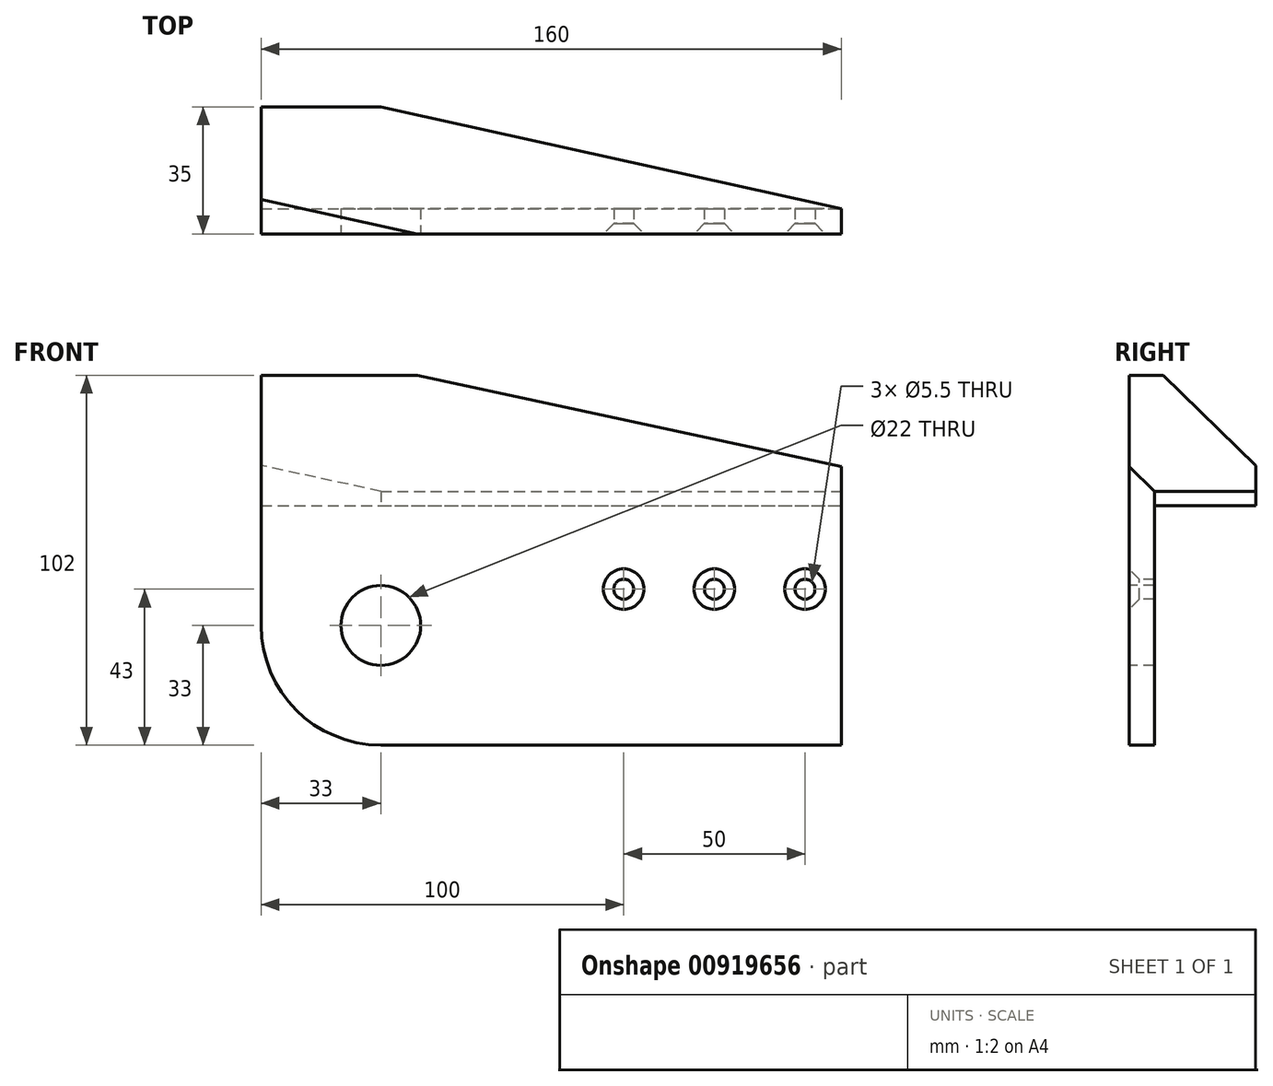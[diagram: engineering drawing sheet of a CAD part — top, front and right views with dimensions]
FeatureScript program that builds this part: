
annotation { "Feature Type Name" : "Feature", "Feature Type Description" : "" }
export const myFeature = defineFeature(function(context is Context, id is Id, definition is map)
    precondition{}
    {
        {
            var Q0;
            Q0=qCreatedBy(makeId("Front.planeOp"),FACE);
            var sketch = newSketch(context, id + "F0", { "sketchPlane" : qUnion([Q0])});
            skCircle(sketch, "E0", {"center": v(0, 0) * mm, "radius": 11 * mm});
            skLineSegment(sketch, "E1", {"start": v(127, -33) * mm, "end": v(0, -33) * mm});
            skLineSegment(sketch, "E2.right", {"start": v(127, 33) * mm, "end": v(127, -33) * mm});
            skLineSegment(sketch, "E3", {"start": v(67, 10) * mm, "end": v(117, 10) * mm, "construction": true});
            skPoint(sketch, "E4", {"position": v(92, 10) * mm});
            skCircle(sketch, "E5", {"center": v(67, 10) * mm, "radius": 2.5 * mm});
            skCircle(sketch, "E6", {"center": v(92, 10) * mm, "radius": 2.5 * mm});
            skCircle(sketch, "E7", {"center": v(117, 10) * mm, "radius": 2.5 * mm});
            skLineSegment(sketch, "E8", {"start": v(-33, 0) * mm, "end": v(-33, 33) * mm});
            skArc(sketch, "E9", {"start": v(0, -33) * mm, "mid": v(-23.33, -23.33) * mm, "end": v(-33, 0) * mm});
            skLineSegment(sketch, "E10", {"start": v(-33, 33) * mm, "end": v(127, 33) * mm});
            skCircle(sketch, "E11", {"center": v(0, 0) * mm, "radius": 33 * mm, "construction": true});
            skSolve(sketch);
        }
        {
            var Q0;
            Q0=makeQuery(id+"F0.imprint","IMPRINT",FACE,{"disambiguationData":[TD([[makeQuery(id+"F0.imprint","IMPRINT",EDGE,{"derivedFrom":sQuery(id+"F0.wireOp",EDGE,"E0")}),-1.0]])]});
            extrude(context, id + "F1", {"entities" : qUnion([Q0]), "oppositeDirection" : true, "depth" : 7 * mm, "offsetDistance" : 25 * mm});
        }
        {
            var Q0;
            Q0=sQuery(id+"F0.wireOp",VERTEX,"E3.end");
            var Q1;
            Q1=sQuery(id+"F0.wireOp",VERTEX,"E4");
            var Q2;
            Q2=sQuery(id+"F0.wireOp",VERTEX,"E3.start");
            var Q3;
            Q3=makeQuery(id+"F1.opExtrude","SWEPT_BODY",BODY,{"disambiguationData":[OSD([sQuery(id+"F0.wireOp",EDGE,"E0"),sQuery(id+"F0.wireOp",EDGE,"NhK39m2a-VStp-sb5Q-2b8d-sSrkkGbPDMdk.bottom"),sQuery(id+"F0.wireOp",EDGE,"Ms3glqPk-d3eh-z7h0-pjau-ro7snqxkULMq"),sQuery(id+"F0.wireOp",EDGE,"E1"),sQuery(id+"F0.wireOp",EDGE,"E2.top"),sQuery(id+"F0.wireOp",EDGE,"E2.right"),sQuery(id+"F0.wireOp",EDGE,"IbDPm6no-YCs2-ccEi-nkeo-IJeqVegaUwix"),sQuery(id+"F0.wireOp",EDGE,"7040a60f-2939-40c3-b32a-edc00388365c.filletArc"),sQuery(id+"F0.wireOp",EDGE,"75141edd-5c34-434d-af1e-d0841e09dd0e.filletArc")])]});
            hole(context, id + "F2", {"style" : HoleStyle.C_SINK, "endStyle" : HoleEndStyle.THROUGH, "standardTappedOrClearance" : lookupTablePath({ "fit" : "Normal", "standard" : "ISO", "size" : "M5", "type" : "Clearance" }), "standardBlindInLast" : lookupTablePath({ "fit" : "Normal", "standard" : "ISO", "engagement" : "75%", "pitch" : "0.8 mm", "size" : "M5", "type" : "Clearance & tapped" }), "holeDiameter" : 5.5 * mm, "cSinkDiameter" : 11.2 * mm, "cSinkAngle" : 90 * degree, "majorDiameter" : 5 * mm, "isTappedThrough" : true, "tappedDepth" : 12 * mm, "tapClearance" : 3, "locations" : qUnion([Q0, Q1, Q2]), "scope" : qUnion([Q3])});
        }
        {
            var Q0;
            Q0=makeQuery(id+"F1.opExtrude","SWEPT_FACE",FACE,{"disambiguationData":[OSD([sQuery(id+"F0.wireOp",EDGE,"E10")])]});
            var sketch = newSketch(context, id + "F3", { "sketchPlane" : qUnion([Q0])});
            skLineSegment(sketch, "E12", {"start": v(-33, 35) * mm, "end": v(-33, 0) * mm});
            skLineSegment(sketch, "E13", {"start": v(-33, 0) * mm, "end": v(127, 0) * mm});
            skLineSegment(sketch, "E14", {"start": v(127, 0) * mm, "end": v(127, 7) * mm});
            skLineSegment(sketch, "E15", {"start": v(-33, 35) * mm, "end": v(0, 35) * mm});
            skLineSegment(sketch, "E16", {"start": v(0, 35) * mm, "end": v(127, 7) * mm});
            skSolve(sketch);
        }
        {
            var Q0;
            Q0 = qSketchRegion(id + "F3", true);
            extrude(context, id + "F4", {"entities" : qUnion([Q0]), "operationType" : NewBodyOperationType.ADD, "depth" : 36 * mm, "offsetDistance" : 25 * mm});
        }
        {
            var Q0;
            Q0=makeQuery(id+"F4.opExtrude","CAP_EDGE",EDGE,{"disambiguationData":[OSD([sQuery(id+"F3.wireOp",EDGE,"E16")])],"isStart":false});
            chamfer(context, id + "F5", {"entities" : qUnion([Q0]), "width" : 32 * mm, "tangentPropagation" : true});
        }
    });
